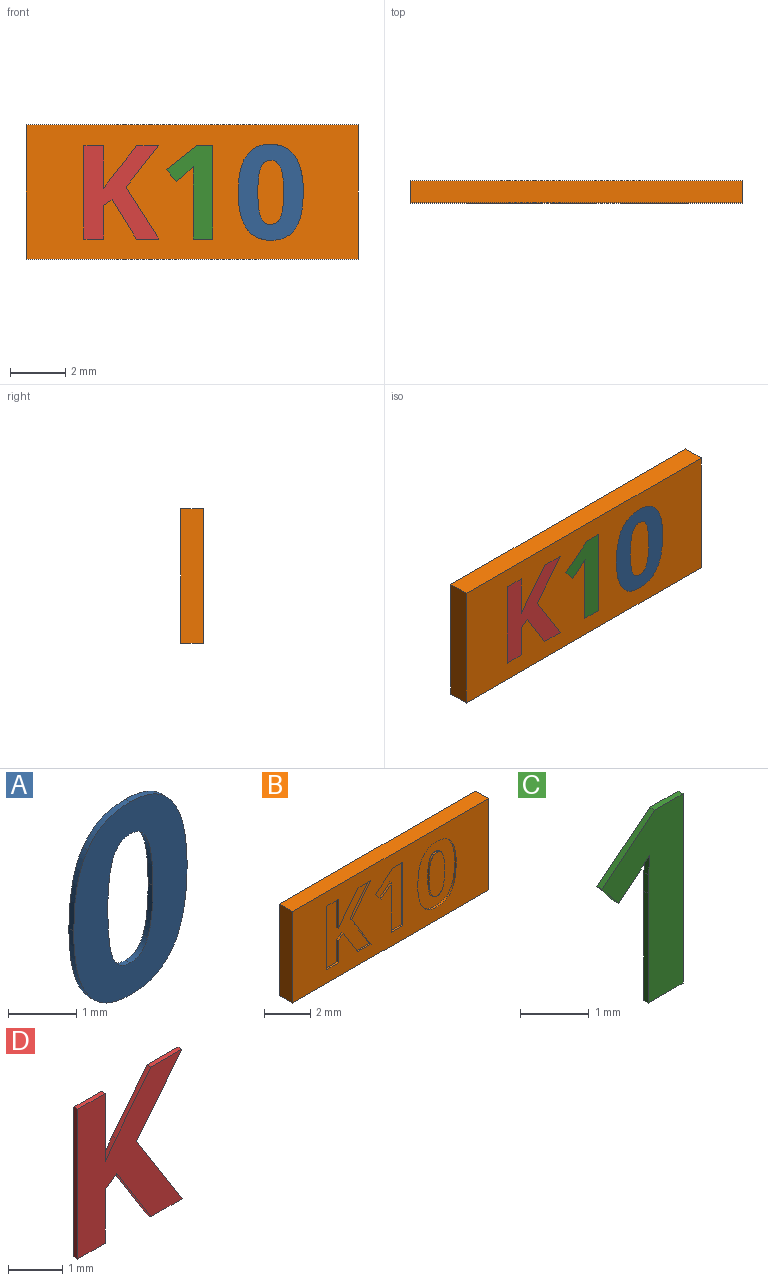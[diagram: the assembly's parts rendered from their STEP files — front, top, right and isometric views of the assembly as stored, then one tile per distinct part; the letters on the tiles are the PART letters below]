
ASSEMBLY  parts=4 mates=3
PART A: 18 faces, bbox 2.4x0.1x3.5 mm
  f0: plane 3.47x2.36mm, normal (0,-1,0), area 5mm2, adj f1,f2,f3,f4,f5,f6,f7,f8
  f1: extruded ~0.88x0.44mm, area 0.1mm2, adj f0,f2,f11,f13
  f2: extruded ~0.89x0.42mm, area 0.1mm2, adj f0,f1,f3,f11
  f3: extruded ~1.32x0.29mm, area 0.1mm2, adj f0,f2,f4,f11
  f4: extruded ~1.29x0.3mm, area 0.1mm2, adj f0,f3,f5,f11
  f5: extruded ~0.88x0.44mm, area 0.1mm2, adj f0,f4,f11,f12
  f6: extruded ~0.36x0.27mm, area 0mm2, adj f0,f7,f11,f16
  f7: extruded ~0.36x0.27mm, area 0mm2, adj f0,f6,f8,f11
  f8: extruded ~0.89x0.11mm, area 0.1mm2, adj f0,f7,f9,f11
  f9: extruded ~0.89x0.11mm, area 0.1mm2, adj f0,f8,f10,f11
  f10: extruded ~0.36x0.27mm, area 0mm2, adj f0,f9,f11,f15
  f11: plane 3.47x2.36mm, normal (0,1,0), area 5mm2, adj f1,f2,f3,f4,f5,f6,f7,f8
  f12: extruded ~0.89x0.42mm, area 0.1mm2, adj f0,f5,f11,f14
  f13: extruded ~1.3x0.3mm, area 0.1mm2, adj f0,f1,f11,f14
  f14: extruded ~1.31x0.29mm, area 0.1mm2, adj f0,f11,f12,f13
  f15: extruded ~0.36x0.27mm, area 0mm2, adj f0,f10,f11,f17
  f16: extruded ~0.89x0.11mm, area 0.1mm2, adj f0,f6,f11,f17
  f17: extruded ~0.89x0.11mm, area 0.1mm2, adj f0,f11,f15,f16
PART B: 49 faces, bbox 12x0.8x4.9 mm
  f0: plane 12x4.85mm, normal (0,-1,0), area 43.2mm2, adj f1,f2,f3,f4,f6,f7,f8,f9
  f1: plane 12x0.8mm, normal (0,0,-1), area 9.6mm2, adj f0,f2,f4,f5
  f2: plane 4.85x0.8mm, normal (1,0,0), area 3.9mm2, adj f0,f1,f3,f5
  f3: plane 12x0.8mm, normal (0,0,1), area 9.6mm2, adj f0,f2,f4,f5
  f4: plane 4.85x0.8mm, normal (-1,0,0), area 3.9mm2, adj f0,f1,f3,f5
  f5: plane 12x4.85mm, normal (0,1,0), area 58.2mm2, adj f1,f2,f3,f4
  f6: extruded ~1.3x0.3mm, area 0.1mm2, adj f0,f7,f21,f22
  f7: extruded ~0.88x0.44mm, area 0.1mm2, adj f0,f6,f8,f22
  f8: extruded ~0.89x0.42mm, area 0.1mm2, adj f0,f7,f9,f22
  f9: extruded ~1.32x0.29mm, area 0.1mm2, adj f0,f8,f10,f22
  f10: extruded ~1.29x0.3mm, area 0.1mm2, adj f0,f9,f11,f22
  f11: extruded ~0.88x0.44mm, area 0.1mm2, adj f0,f10,f12,f22
  f12: extruded ~0.89x0.42mm, area 0.1mm2, adj f0,f11,f21,f22
  f13: extruded ~0.89x0.11mm, area 0.1mm2, adj f14,f20,f22,f23
  f14: extruded ~0.36x0.27mm, area 0mm2, adj f13,f15,f22,f23
  f15: extruded ~0.36x0.27mm, area 0mm2, adj f14,f16,f22,f23
  f16: extruded ~0.89x0.11mm, area 0.1mm2, adj f15,f17,f22,f23
  f17: extruded ~0.89x0.11mm, area 0.1mm2, adj f16,f18,f22,f23
  f18: extruded ~0.36x0.27mm, area 0mm2, adj f17,f19,f22,f23
  f19: extruded ~0.36x0.27mm, area 0mm2, adj f18,f20,f22,f23
  f20: extruded ~0.89x0.11mm, area 0.1mm2, adj f13,f19,f22,f23
  f21: extruded ~1.31x0.29mm, area 0.1mm2, adj f0,f6,f12,f22
  f22: plane 3.47x2.36mm, normal (0,-1,0), area 5mm2, adj f6,f7,f8,f9,f10,f11,f12,f13
  f23: plane 2.32x0.94mm, normal (0,-1,0), area 1.8mm2, adj f13,f14,f15,f16,f17,f18,f19,f20
  f24: plane 3.37x0.1mm, normal (-1,0,0), area 0.3mm2, adj f0,f25,f33,f34
  f25: plane 0.59x0.1mm, normal (0,0,-1), area 0.1mm2, adj f0,f24,f26,f34
  f26: plane 1.09x0.86mm, normal (0.62,0,-0.78), area 0.1mm2, adj f0,f25,f27,f34
  f27: plane 0.43x0.34mm, normal (0.78,0,0.63), area 0.1mm2, adj f0,f26,f28,f34
  f28: plane 0.39x0.31mm, normal (-0.63,0,0.78), area 0mm2, adj f0,f27,f29,f34
  f29: extruded ~0.25x0.23mm, area 0mm2, adj f0,f28,f30,f34
  f30: plane 0.35x0.1mm, normal (1,0,-0.03), area 0mm2, adj f0,f29,f31,f34
  f31: plane 0.32x0.1mm, normal (1,0,-0.02), area 0mm2, adj f0,f30,f32,f34
  f32: plane 1.95x0.1mm, normal (1,0,0), area 0.2mm2, adj f0,f31,f33,f34
  f33: plane 0.71x0.1mm, normal (0,0,1), area 0.1mm2, adj f0,f24,f32,f34
  f34: plane 3.37x1.67mm, normal (0,-1,0), area 2.9mm2, adj f24,f25,f26,f27,f28,f29,f30,f31
  f35: plane 1.88x1.19mm, normal (-0.85,0,-0.53), area 0.2mm2, adj f0,f36,f47,f48
  f36: plane 1.49x1.18mm, normal (-0.79,0,0.62), area 0.2mm2, adj f0,f35,f37,f48
  f37: plane 0.79x0.1mm, normal (0,0,-1), area 0.1mm2, adj f0,f36,f38,f48
  f38: plane 1.15x0.91mm, normal (0.78,0,-0.62), area 0.1mm2, adj f0,f37,f39,f48
  f39: plane 0.4x0.28mm, normal (0.82,0,-0.58), area 0mm2, adj f0,f38,f40,f48
  f40: plane 1.54x0.1mm, normal (-1,0,0), area 0.2mm2, adj f0,f39,f41,f48
  f41: plane 0.72x0.1mm, normal (0,0,-1), area 0.1mm2, adj f0,f40,f42,f48
  f42: plane 3.37x0.1mm, normal (1,0,0), area 0.3mm2, adj f0,f41,f43,f48
  f43: plane 0.72x0.1mm, normal (0,0,1), area 0.1mm2, adj f0,f42,f44,f48
  f44: plane 1.2x0.1mm, normal (-1,0,0), area 0.1mm2, adj f0,f43,f45,f48
  f45: plane 0.3x0.22mm, normal (-0.58,0,0.81), area 0mm2, adj f0,f44,f46,f48
  f46: plane 1.42x0.88mm, normal (0.85,0,0.53), area 0.2mm2, adj f0,f45,f47,f48
  f47: plane 0.81x0.1mm, normal (0,0,1), area 0.1mm2, adj f0,f35,f46,f48
  f48: plane 3.37x2.71mm, normal (0,-1,0), area 5.2mm2, adj f35,f36,f37,f38,f39,f40,f41,f42
PART C: 12 faces, bbox 1.7x0.1x3.4 mm
  f0: plane 3.37x1.67mm, normal (0,-1,0), area 2.9mm2, adj f1,f2,f3,f4,f5,f6,f7,f9
  f1: plane 0.59x0.1mm, normal (0,0,1), area 0.1mm2, adj f0,f2,f8,f10
  f2: plane 1.09x0.86mm, normal (-0.62,0,0.78), area 0.1mm2, adj f0,f1,f3,f8
  f3: plane 0.43x0.34mm, normal (-0.78,0,-0.63), area 0.1mm2, adj f0,f2,f4,f8
  f4: plane 0.39x0.31mm, normal (0.63,0,-0.78), area 0mm2, adj f0,f3,f5,f8
  f5: extruded ~0.25x0.23mm, area 0mm2, adj f0,f4,f6,f8
  f6: plane 0.35x0.1mm, normal (-1,0,0.03), area 0mm2, adj f0,f5,f7,f8
  f7: plane 0.32x0.1mm, normal (-1,0,0.02), area 0mm2, adj f0,f6,f8,f9
  f8: plane 3.37x1.67mm, normal (0,1,0), area 2.9mm2, adj f1,f2,f3,f4,f5,f6,f7,f9
  f9: plane 1.95x0.1mm, normal (-1,0,0), area 0.2mm2, adj f0,f7,f8,f11
  f10: plane 3.37x0.1mm, normal (1,0,0), area 0.3mm2, adj f0,f1,f8,f11
  f11: plane 0.71x0.1mm, normal (0,0,-1), area 0.1mm2, adj f0,f8,f9,f10
PART D: 15 faces, bbox 2.7x0.1x3.4 mm
  f0: plane 3.37x2.71mm, normal (0,-1,0), area 5.2mm2, adj f1,f2,f3,f4,f5,f6,f7,f8
  f1: plane 1.49x1.18mm, normal (0.79,0,-0.62), area 0.2mm2, adj f0,f2,f11,f13
  f2: plane 0.79x0.1mm, normal (0,0,1), area 0.1mm2, adj f0,f1,f3,f11
  f3: plane 1.15x0.91mm, normal (-0.78,0,0.62), area 0.1mm2, adj f0,f2,f4,f11
  f4: plane 0.4x0.28mm, normal (-0.82,0,0.58), area 0mm2, adj f0,f3,f5,f11
  f5: plane 1.54x0.1mm, normal (1,0,0), area 0.2mm2, adj f0,f4,f6,f11
  f6: plane 0.72x0.1mm, normal (0,0,1), area 0.1mm2, adj f0,f5,f7,f11
  f7: plane 3.37x0.1mm, normal (-1,0,0), area 0.3mm2, adj f0,f6,f8,f11
  f8: plane 0.72x0.1mm, normal (0,0,-1), area 0.1mm2, adj f0,f7,f9,f11
  f9: plane 1.2x0.1mm, normal (1,0,0), area 0.1mm2, adj f0,f8,f10,f11
  f10: plane 0.3x0.22mm, normal (0.58,0,-0.81), area 0mm2, adj f0,f9,f11,f12
  f11: plane 3.37x2.71mm, normal (0,1,0), area 5.2mm2, adj f1,f2,f3,f4,f5,f6,f7,f8
  f12: plane 1.42x0.88mm, normal (-0.85,0,-0.53), area 0.2mm2, adj f0,f10,f11,f14
  f13: plane 1.88x1.19mm, normal (0.85,0,0.53), area 0.2mm2, adj f0,f1,f11,f14
  f14: plane 0.81x0.1mm, normal (0,0,-1), area 0.1mm2, adj f0,f11,f12,f13
PLACE A t=(-0.02,0.4,0)mm
PLACE B t=(-0.02,0.4,0)mm
PLACE C t=(-1.66,0.4,0)mm
PLACE D t=(-1.66,0.4,0)mm
MATE fastened A.f0 <-> B.f0  axis (0,-1,0) through (2.82,-0.4,-1.75)mm
MATE fastened D.f0 <-> B.f0  axis (0,-1,0) through (-3.93,-0.4,-1.7)mm
MATE fastened C.f0 <-> B.f0  axis (0,-1,0) through (0.02,-0.4,-1.7)mm
